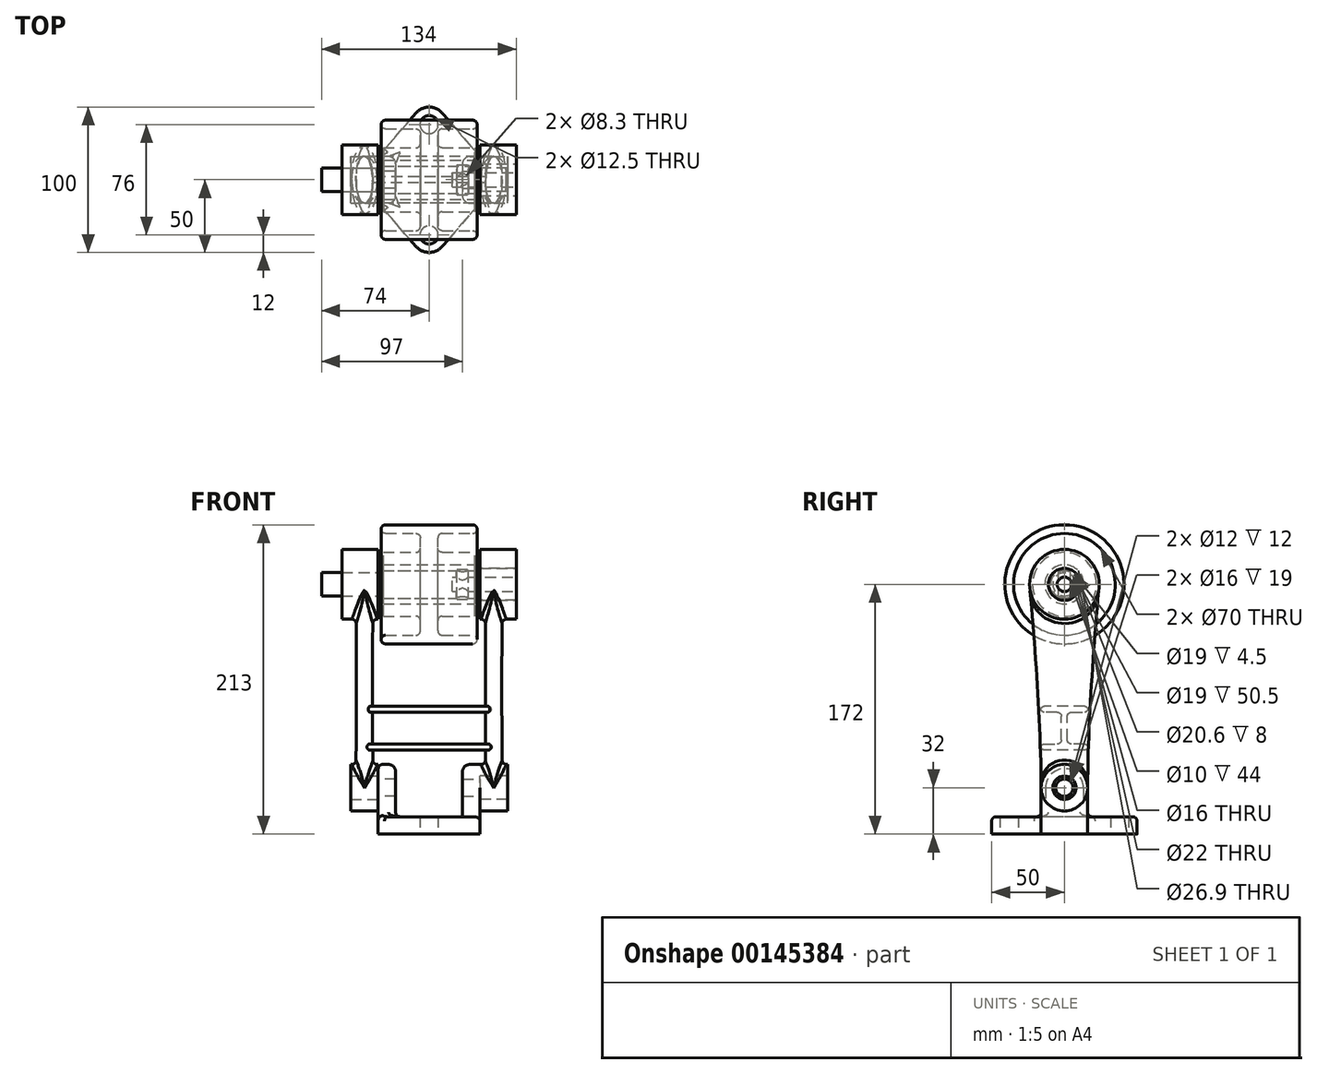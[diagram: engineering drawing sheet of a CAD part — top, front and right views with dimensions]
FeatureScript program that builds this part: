
annotation { "Feature Type Name" : "Feature", "Feature Type Description" : "" }
export const myFeature = defineFeature(function(context is Context, id is Id, definition is map)
    precondition{}
    {
        {
            var Q0;
            Q0=qCreatedBy(makeId("Top.planeOp"),FACE);
            var sketch = newSketch(context, id + "F0", { "sketchPlane" : qUnion([Q0])});
            skLineSegment(sketch, "E0", {"start": v(-9.06, -45.87) * mm, "end": v(-35, -16) * mm});
            skLineSegment(sketch, "E1", {"start": v(-35, 16) * mm, "end": v(-9.06, 45.87) * mm});
            skLineSegment(sketch, "E2", {"start": v(9.06, 45.87) * mm, "end": v(35, 16) * mm});
            skLineSegment(sketch, "E3", {"start": v(35, -16) * mm, "end": v(9.06, -45.87) * mm});
            skLineSegment(sketch, "E4", {"start": v(35, -16) * mm, "end": v(35, 16) * mm});
            skLineSegment(sketch, "E5", {"start": v(-35, -16) * mm, "end": v(-35, 16) * mm});
            skPoint(sketch, "E6.orphan", {"position": v(-48.9, 0) * mm});
            skPoint(sketch, "E7.orphan", {"position": v(48.9, 0) * mm});
            skPoint(sketch, "E8.visualSharp", {"position": v(0, -56.3) * mm});
            skArc(sketch, "E8.filletArc", {"start": v(-9.06, -45.87) * mm, "mid": v(0, -50) * mm, "end": v(9.06, -45.87) * mm});
            skPoint(sketch, "E9.visualSharp", {"position": v(0, 56.3) * mm});
            skArc(sketch, "E9.filletArc", {"start": v(9.06, 45.87) * mm, "mid": v(0, 50) * mm, "end": v(-9.06, 45.87) * mm});
            skCircle(sketch, "E10", {"center": v(0, -38) * mm, "radius": 6.25 * mm});
            skCircle(sketch, "E11", {"center": v(0, 38) * mm, "radius": 6.25 * mm});
            skSolve(sketch);
        }
        {
            var Q0;
            Q0=qSketchRegion(id+"F0",true);
            extrude(context, id + "F1", {"entities" : qUnion([Q0]), "depth" : 12 * mm});
        }
        {
            var Q0;
            Q0=makeQuery(id+"F1.opExtrude","SWEPT_FACE",FACE,{"disambiguationData":[OSD([sQuery(id+"F0.wireOp",EDGE,"E5")])]});
            var sketch = newSketch(context, id + "F2", { "sketchPlane" : qUnion([Q0])});
            skLineSegment(sketch, "E12", {"start": v(-16, 0) * mm, "end": v(-16, 32) * mm});
            skLineSegment(sketch, "E13", {"start": v(16, 0) * mm, "end": v(16, 32) * mm});
            skArc(sketch, "E14", {"start": v(16, 32) * mm, "mid": v(0, 48) * mm, "end": v(-16, 32) * mm});
            skLineSegment(sketch, "E15", {"start": v(-16, 0) * mm, "end": v(16, 0) * mm});
            skCircle(sketch, "E16", {"center": v(0, 32) * mm, "radius": 6 * mm});
            skSolve(sketch);
        }
        {
            var Q0;
            Q0=qSketchRegion(id+"F2",true);
            extrude(context, id + "F3", {"entities" : qUnion([Q0]), "operationType" : NewBodyOperationType.ADD, "oppositeDirection" : true, "depth" : 12 * mm});
        }
        {
            var Q0;
            Q0=makeQuery(id+"F1.opExtrude","SWEPT_BODY",BODY,{"disambiguationData":[OSD([sQuery(id+"F0.wireOp",EDGE,"E0"),sQuery(id+"F0.wireOp",EDGE,"E1"),sQuery(id+"F0.wireOp",EDGE,"E2"),sQuery(id+"F0.wireOp",EDGE,"E3"),sQuery(id+"F0.wireOp",EDGE,"E4"),sQuery(id+"F0.wireOp",EDGE,"E5"),sQuery(id+"F0.wireOp",EDGE,"E8.filletArc"),sQuery(id+"F0.wireOp",EDGE,"E9.filletArc"),sQuery(id+"F0.wireOp",EDGE,"E10"),sQuery(id+"F0.wireOp",EDGE,"E11")])]});
            var Q1;
            Q1=qCreatedBy(makeId("Right.planeOp"),FACE);
            mirror(context, id + "F4", {"operationType" : NewBodyOperationType.ADD, "entities" : qUnion([Q0]), "mirrorPlane" : qUnion([Q1])});
        }
        {
            var Q0;
            Q0=makeQuery(id+"F4.opPattern","COPY",EDGE,{"derivedFrom":makeQuery(id+"F3.boolean.opBoolean","INTERSECT",EDGE,{"derivedFrom":[makeQuery(id+"F1.opExtrude","CAP_FACE",FACE,{"disambiguationData":[OSD([sQuery(id+"F0.wireOp",EDGE,"E0"),sQuery(id+"F0.wireOp",EDGE,"E1"),sQuery(id+"F0.wireOp",EDGE,"E2"),sQuery(id+"F0.wireOp",EDGE,"E3"),sQuery(id+"F0.wireOp",EDGE,"E4"),sQuery(id+"F0.wireOp",EDGE,"E5"),sQuery(id+"F0.wireOp",EDGE,"E8.filletArc"),sQuery(id+"F0.wireOp",EDGE,"E9.filletArc"),sQuery(id+"F0.wireOp",EDGE,"E10"),sQuery(id+"F0.wireOp",EDGE,"E11")])],"isStart":false}),makeQuery(id+"F3.opExtrude","SWEPT_FACE",FACE,{"disambiguationData":[OSD([sQuery(id+"F2.wireOp",EDGE,"E12")])]})]}),"instanceName":"1"});
            var Q1;
            Q1=makeQuery(id+"F4.opPattern","COPY",EDGE,{"derivedFrom":makeQuery(id+"F3.boolean.opBoolean","INTERSECT",EDGE,{"derivedFrom":[makeQuery(id+"F1.opExtrude","CAP_FACE",FACE,{"disambiguationData":[OSD([sQuery(id+"F0.wireOp",EDGE,"E0"),sQuery(id+"F0.wireOp",EDGE,"E1"),sQuery(id+"F0.wireOp",EDGE,"E2"),sQuery(id+"F0.wireOp",EDGE,"E3"),sQuery(id+"F0.wireOp",EDGE,"E4"),sQuery(id+"F0.wireOp",EDGE,"E5"),sQuery(id+"F0.wireOp",EDGE,"E8.filletArc"),sQuery(id+"F0.wireOp",EDGE,"E9.filletArc"),sQuery(id+"F0.wireOp",EDGE,"E10"),sQuery(id+"F0.wireOp",EDGE,"E11")])],"isStart":false}),makeQuery(id+"F3.opExtrude","CAP_FACE",FACE,{"disambiguationData":[OSD([sQuery(id+"F2.wireOp",EDGE,"E12"),sQuery(id+"F2.wireOp",EDGE,"E13"),sQuery(id+"F2.wireOp",EDGE,"E14"),sQuery(id+"F2.wireOp",EDGE,"E15"),sQuery(id+"F2.wireOp",EDGE,"E16")])],"isStart":false})]}),"instanceName":"1"});
            var Q2;
            Q2=makeQuery(id+"F4.opPattern","COPY",EDGE,{"derivedFrom":makeQuery(id+"F3.boolean.opBoolean","INTERSECT",EDGE,{"derivedFrom":[makeQuery(id+"F1.opExtrude","CAP_FACE",FACE,{"disambiguationData":[OSD([sQuery(id+"F0.wireOp",EDGE,"E0"),sQuery(id+"F0.wireOp",EDGE,"E1"),sQuery(id+"F0.wireOp",EDGE,"E2"),sQuery(id+"F0.wireOp",EDGE,"E3"),sQuery(id+"F0.wireOp",EDGE,"E4"),sQuery(id+"F0.wireOp",EDGE,"E5"),sQuery(id+"F0.wireOp",EDGE,"E8.filletArc"),sQuery(id+"F0.wireOp",EDGE,"E9.filletArc"),sQuery(id+"F0.wireOp",EDGE,"E10"),sQuery(id+"F0.wireOp",EDGE,"E11")])],"isStart":false}),makeQuery(id+"F3.opExtrude","SWEPT_FACE",FACE,{"disambiguationData":[OSD([sQuery(id+"F2.wireOp",EDGE,"E13")])]})]}),"instanceName":"1"});
            var Q3;
            Q3=makeQuery(id+"F3.boolean.opBoolean","INTERSECT",EDGE,{"derivedFrom":[makeQuery(id+"F1.opExtrude","CAP_FACE",FACE,{"disambiguationData":[OSD([sQuery(id+"F0.wireOp",EDGE,"E0"),sQuery(id+"F0.wireOp",EDGE,"E1"),sQuery(id+"F0.wireOp",EDGE,"E2"),sQuery(id+"F0.wireOp",EDGE,"E3"),sQuery(id+"F0.wireOp",EDGE,"E4"),sQuery(id+"F0.wireOp",EDGE,"E5"),sQuery(id+"F0.wireOp",EDGE,"E8.filletArc"),sQuery(id+"F0.wireOp",EDGE,"E9.filletArc"),sQuery(id+"F0.wireOp",EDGE,"E10"),sQuery(id+"F0.wireOp",EDGE,"E11")])],"isStart":false}),makeQuery(id+"F3.opExtrude","SWEPT_FACE",FACE,{"disambiguationData":[OSD([sQuery(id+"F2.wireOp",EDGE,"E13")])]})]});
            var Q4;
            Q4=makeQuery(id+"F3.boolean.opBoolean","INTERSECT",EDGE,{"derivedFrom":[makeQuery(id+"F1.opExtrude","CAP_FACE",FACE,{"disambiguationData":[OSD([sQuery(id+"F0.wireOp",EDGE,"E0"),sQuery(id+"F0.wireOp",EDGE,"E1"),sQuery(id+"F0.wireOp",EDGE,"E2"),sQuery(id+"F0.wireOp",EDGE,"E3"),sQuery(id+"F0.wireOp",EDGE,"E4"),sQuery(id+"F0.wireOp",EDGE,"E5"),sQuery(id+"F0.wireOp",EDGE,"E8.filletArc"),sQuery(id+"F0.wireOp",EDGE,"E9.filletArc"),sQuery(id+"F0.wireOp",EDGE,"E10"),sQuery(id+"F0.wireOp",EDGE,"E11")])],"isStart":false}),makeQuery(id+"F3.opExtrude","CAP_FACE",FACE,{"disambiguationData":[OSD([sQuery(id+"F2.wireOp",EDGE,"E12"),sQuery(id+"F2.wireOp",EDGE,"E13"),sQuery(id+"F2.wireOp",EDGE,"E14"),sQuery(id+"F2.wireOp",EDGE,"E15"),sQuery(id+"F2.wireOp",EDGE,"E16")])],"isStart":false})]});
            var Q5;
            Q5=makeQuery(id+"F3.boolean.opBoolean","INTERSECT",EDGE,{"derivedFrom":[makeQuery(id+"F1.opExtrude","CAP_FACE",FACE,{"disambiguationData":[OSD([sQuery(id+"F0.wireOp",EDGE,"E0"),sQuery(id+"F0.wireOp",EDGE,"E1"),sQuery(id+"F0.wireOp",EDGE,"E2"),sQuery(id+"F0.wireOp",EDGE,"E3"),sQuery(id+"F0.wireOp",EDGE,"E4"),sQuery(id+"F0.wireOp",EDGE,"E5"),sQuery(id+"F0.wireOp",EDGE,"E8.filletArc"),sQuery(id+"F0.wireOp",EDGE,"E9.filletArc"),sQuery(id+"F0.wireOp",EDGE,"E10"),sQuery(id+"F0.wireOp",EDGE,"E11")])],"isStart":false}),makeQuery(id+"F3.opExtrude","SWEPT_FACE",FACE,{"disambiguationData":[OSD([sQuery(id+"F2.wireOp",EDGE,"E12")])]})]});
            fillet(context, id + "F5", {"entities" : qUnion([Q0, Q1, Q2, Q3, Q4, Q5]), "radius" : 3 * mm, "tangentPropagation" : true, "allowEdgeOverflow" : false});
        }
        {
            var Q0;
            Q0=makeQuery(id+"F1.opExtrude","CAP_EDGE",EDGE,{"disambiguationData":[OSD([sQuery(id+"F0.wireOp",EDGE,"E1")])],"isStart":false});
            var Q1;
            Q1=makeQuery(id+"F1.opExtrude","CAP_EDGE",EDGE,{"disambiguationData":[OSD([sQuery(id+"F0.wireOp",EDGE,"E0")])],"isStart":false});
            fillet(context, id + "F6", {"entities" : qUnion([Q0, Q1]), "radius" : 3 * mm, "tangentPropagation" : true, "allowEdgeOverflow" : false});
        }
        {
            var Q0;
            Q0=makeQuery(id+"F4.opPattern","COPY",EDGE,{"derivedFrom":makeQuery(id+"F3.opExtrude","CAP_EDGE",EDGE,{"disambiguationData":[OSD([sQuery(id+"F2.wireOp",EDGE,"E14")])],"isStart":false}),"instanceName":"1"});
            var Q1;
            Q1=makeQuery(id+"F3.opExtrude","CAP_EDGE",EDGE,{"disambiguationData":[OSD([sQuery(id+"F2.wireOp",EDGE,"E14")])],"isStart":false});
            fillet(context, id + "F7", {"entities" : qUnion([Q0, Q1]), "radius" : 5 * mm, "tangentPropagation" : true, "allowEdgeOverflow" : false});
        }
        {
            var Q0;
            Q0=makeQuery(id+"F4.boolean.opBoolean","MERGE",FACE,{"derivedFrom":[makeQuery(id+"F1.opExtrude","SWEPT_FACE",FACE,{"disambiguationData":[OSD([sQuery(id+"F0.wireOp",EDGE,"E4")])]}),makeQuery(id+"F4.opPattern","COPY",FACE,{"derivedFrom":makeQuery(id+"F3.boolean.opBoolean","MERGE",FACE,{"derivedFrom":[makeQuery(id+"F1.opExtrude","SWEPT_FACE",FACE,{"disambiguationData":[OSD([sQuery(id+"F0.wireOp",EDGE,"E5")])]}),makeQuery(id+"F3.opExtrude","CAP_FACE",FACE,{"disambiguationData":[OSD([sQuery(id+"F2.wireOp",EDGE,"E12"),sQuery(id+"F2.wireOp",EDGE,"E13"),sQuery(id+"F2.wireOp",EDGE,"E14"),sQuery(id+"F2.wireOp",EDGE,"E15"),sQuery(id+"F2.wireOp",EDGE,"E16")])],"isStart":true})]}),"instanceName":"1"})]});
            var sketch = newSketch(context, id + "F8", { "sketchPlane" : qUnion([Q0])});
            skCircle(sketch, "E17", {"center": v(0, 32) * mm, "radius": 8 * mm});
            skCircle(sketch, "E18", {"center": v(0, 32) * mm, "radius": 16 * mm});
            skSolve(sketch);
        }
        {
            var Q0;
            Q0=qSketchRegion(id+"F8",true);
            extrude(context, id + "F9", {"entities" : qUnion([Q0]), "depth" : 19 * mm});
        }
        {
            var Q0;
            Q0=makeQuery(id+"F4.boolean.opBoolean","MERGE",FACE,{"derivedFrom":[makeQuery(id+"F1.opExtrude","SWEPT_FACE",FACE,{"disambiguationData":[OSD([sQuery(id+"F0.wireOp",EDGE,"E4")])]}),makeQuery(id+"F4.opPattern","COPY",FACE,{"derivedFrom":makeQuery(id+"F3.boolean.opBoolean","MERGE",FACE,{"derivedFrom":[makeQuery(id+"F1.opExtrude","SWEPT_FACE",FACE,{"disambiguationData":[OSD([sQuery(id+"F0.wireOp",EDGE,"E5")])]}),makeQuery(id+"F3.opExtrude","CAP_FACE",FACE,{"disambiguationData":[OSD([sQuery(id+"F2.wireOp",EDGE,"E12"),sQuery(id+"F2.wireOp",EDGE,"E13"),sQuery(id+"F2.wireOp",EDGE,"E14"),sQuery(id+"F2.wireOp",EDGE,"E15"),sQuery(id+"F2.wireOp",EDGE,"E16")])],"isStart":true})]}),"instanceName":"1"})]});
            var sketch = newSketch(context, id + "F10", { "sketchPlane" : qUnion([Q0])});
            skCircle(sketch, "E19", {"center": v(0, 172) * mm, "radius": 8 * mm});
            skCircle(sketch, "E20", {"center": v(0, 172) * mm, "radius": 24 * mm});
            skSolve(sketch);
        }
        {
            var Q0;
            Q0=qSketchRegion(id+"F10",true);
            extrude(context, id + "F11", {"entities" : qUnion([Q0]), "depth" : 25 * mm});
        }
        {
            var Q0;
            Q0=qCreatedBy(makeId("Top.planeOp"),FACE);
            var Q1;
            Q1=sQuery(id+"F2.wireOp",VERTEX,"E14.center");
            cPlane(context, id + "F12", {"entities" : qUnion([Q0, Q1]), "cplaneType" : CPlaneType.PLANE_POINT, "offset" : 25 * mm, "width" : 150 * mm, "height" : 150 * mm});
        }
        {
            var Q0;
            Q0=qCreatedBy(id+"F12.planeOp",FACE);
            var sketch = newSketch(context, id + "F13", { "sketchPlane" : qUnion([Q0])});
            skEllipse(sketch, "E21", {"center": v(44.5, 0) * mm, "majorRadius": 16 * mm, "minorRadius": 6 * mm, "majorAxis": v(0, -1)});
            skSolve(sketch);
        }
        {
            var Q0;
            Q0=makeQuery(id+"F4.boolean.opBoolean","MERGE",FACE,{"derivedFrom":[makeQuery(id+"F1.opExtrude","SWEPT_FACE",FACE,{"disambiguationData":[OSD([sQuery(id+"F0.wireOp",EDGE,"E4")])]}),makeQuery(id+"F4.opPattern","COPY",FACE,{"derivedFrom":makeQuery(id+"F3.boolean.opBoolean","MERGE",FACE,{"derivedFrom":[makeQuery(id+"F1.opExtrude","SWEPT_FACE",FACE,{"disambiguationData":[OSD([sQuery(id+"F0.wireOp",EDGE,"E5")])]}),makeQuery(id+"F3.opExtrude","CAP_FACE",FACE,{"disambiguationData":[OSD([sQuery(id+"F2.wireOp",EDGE,"E12"),sQuery(id+"F2.wireOp",EDGE,"E13"),sQuery(id+"F2.wireOp",EDGE,"E14"),sQuery(id+"F2.wireOp",EDGE,"E15"),sQuery(id+"F2.wireOp",EDGE,"E16")])],"isStart":true})]}),"instanceName":"1"})]});
            var sketch = newSketch(context, id + "F14", { "sketchPlane" : qUnion([Q0])});
            skCircle(sketch, "E22.0", {"center": v(0, 32) * mm, "radius": 8 * mm});
            skSolve(sketch);
        }
        {
            var Q0;
            Q0=makeQuery(id+"F14.imprint","IMPRINT",FACE,{"disambiguationData":[TD([[makeQuery(id+"F14.imprint","IMPRINT",EDGE,{"derivedFrom":sQuery(id+"F14.wireOp",EDGE,"E22.0")}),-1.0]])]});
            var sketch = newSketch(context, id + "F15", { "sketchPlane" : qUnion([Q0])});
            skCircle(sketch, "E23.0", {"center": v(0, 32) * mm, "radius": 8 * mm});
            skSolve(sketch);
        }
        {
            var Q0;
            Q0=qSketchRegion(id+"F15",true);
            extrude(context, id + "F16", {"entities" : qUnion([Q0]), "operationType" : NewBodyOperationType.REMOVE, "depth" : 25 * mm});
        }
        {
            var Q0;
            Q0=qCreatedBy(id+"F12.planeOp",FACE);
            var Q1;
            Q1=sQuery(id+"F10.wireOp",VERTEX,"E19.center");
            cPlane(context, id + "F17", {"entities" : qUnion([Q0, Q1]), "cplaneType" : CPlaneType.PLANE_POINT, "offset" : 25 * mm, "width" : 150 * mm, "height" : 150 * mm});
        }
        {
            var Q0;
            Q0=qCreatedBy(id+"F17.planeOp",FACE);
            var sketch = newSketch(context, id + "F18", { "sketchPlane" : qUnion([Q0])});
            skEllipse(sketch, "E24", {"center": v(44.5, 0) * mm, "majorRadius": 24 * mm, "minorRadius": 6 * mm, "majorAxis": v(0, 1)});
            skSolve(sketch);
        }
        {
            var Q0;
            Q0=qSketchRegion(id+"F13",true);
            var Q1;
            Q1=qSketchRegion(id+"F18",true);
            loft(context, id + "F19", {"operationType" : NewBodyOperationType.ADD, "sheetProfilesArray" : [{ "sheetProfileEntities" : qUnion([Q0]) }, { "sheetProfileEntities" : qUnion([Q1]) }]});
        }
        {
            var Q0;
            Q0=makeQuery(id+"F11.opExtrude","CAP_FACE",FACE,{"disambiguationData":[OSD([sQuery(id+"F10.wireOp",EDGE,"E19"),sQuery(id+"F10.wireOp",EDGE,"E20")])],"isStart":false});
            var sketch = newSketch(context, id + "F20", { "sketchPlane" : qUnion([Q0])});
            skCircle(sketch, "E25.0", {"center": v(0, 172) * mm, "radius": 8 * mm});
            skSolve(sketch);
        }
        {
            var Q0;
            Q0=qSketchRegion(id+"F20",true);
            extrude(context, id + "F21", {"entities" : qUnion([Q0]), "operationType" : NewBodyOperationType.REMOVE, "endBound" : BoundingType.THROUGH_ALL, "oppositeDirection" : true, "depth" : 25 * mm});
        }
        {
            var Q0;
            Q0=makeQuery(id+"F9.opExtrude","CAP_FACE",FACE,{"disambiguationData":[OSD([sQuery(id+"F8.wireOp",EDGE,"E17"),sQuery(id+"F8.wireOp",EDGE,"E18")])],"isStart":true});
            var sketch = newSketch(context, id + "F22", { "sketchPlane" : qUnion([Q0])});
            skCircle(sketch, "E26.0", {"center": v(0, 32) * mm, "radius": 8 * mm});
            skSolve(sketch);
        }
        {
            var Q0;
            Q0=qSketchRegion(id+"F22",true);
            extrude(context, id + "F23", {"entities" : qUnion([Q0]), "operationType" : NewBodyOperationType.REMOVE, "oppositeDirection" : true, "depth" : 25 * mm});
        }
        {
            var Q0;
            Q0=qCreatedBy(makeId("Right.planeOp"),FACE);
            var sketch = newSketch(context, id + "F24", { "sketchPlane" : qUnion([Q0])});
            skLineSegment(sketch, "E27", {"start": v(0, 88) * mm, "end": v(14, 88) * mm});
            skLineSegment(sketch, "E28", {"start": v(14, 84) * mm, "end": v(5, 84) * mm});
            skLineSegment(sketch, "E29", {"start": v(2, 81) * mm, "end": v(2, 65) * mm});
            skLineSegment(sketch, "E30", {"start": v(5, 62) * mm, "end": v(14, 62) * mm});
            skLineSegment(sketch, "E31", {"start": v(14, 58) * mm, "end": v(0, 58) * mm});
            skArc(sketch, "E32", {"start": v(14, 84) * mm, "mid": v(16, 86) * mm, "end": v(14, 88) * mm});
            skArc(sketch, "E33", {"start": v(14, 58) * mm, "mid": v(16, 60) * mm, "end": v(14, 62) * mm});
            skPoint(sketch, "E34.visualSharp", {"position": v(2, 84) * mm});
            skArc(sketch, "E34.filletArc", {"start": v(5, 84) * mm, "mid": v(2.88, 83.12) * mm, "end": v(2, 81) * mm});
            skPoint(sketch, "E35.visualSharp", {"position": v(2, 62) * mm});
            skArc(sketch, "E35.filletArc", {"start": v(2, 65) * mm, "mid": v(2.88, 62.88) * mm, "end": v(5, 62) * mm});
            skPoint(sketch, "E36.visualSharp", {"position": v(-2, 62) * mm});
            skPoint(sketch, "E37.visualSharp", {"position": v(-2, 84) * mm});
            skLineSegment(sketch, "E38", {"start": v(0, 32) * mm, "end": v(0, 94.51) * mm, "construction": true});
            skPoint(sketch, "E39.start.orphan", {"position": v(-16, 88) * mm});
            skPoint(sketch, "E40.end.orphan", {"position": v(-16, 84) * mm});
            skPoint(sketch, "E41.end.orphan", {"position": v(-16, 58) * mm});
            skPoint(sketch, "E41.start.orphan", {"position": v(-16, 62) * mm});
            skArc(sketch, "E42.MirrorCS", {"start": v(-2, 65) * mm, "mid": v(-2.88, 62.88) * mm, "end": v(-5, 62) * mm});
            skArc(sketch, "E43.MirrorCS", {"start": v(-5, 84) * mm, "mid": v(-2.88, 83.12) * mm, "end": v(-2, 81) * mm});
            skPoint(sketch, "E44.MirrorP", {"position": v(16, 84) * mm});
            skArc(sketch, "E45.MirrorCS", {"start": v(-14, 84) * mm, "mid": v(-16, 86) * mm, "end": v(-14, 88) * mm});
            skArc(sketch, "E46.MirrorCS", {"start": v(-14, 58) * mm, "mid": v(-16, 60) * mm, "end": v(-14, 62) * mm});
            skLineSegment(sketch, "E47.MirrorCS", {"start": v(-14, 58) * mm, "end": v(0, 58) * mm});
            skLineSegment(sketch, "E48.MirrorCS", {"start": v(0, 88) * mm, "end": v(-14, 88) * mm});
            skLineSegment(sketch, "E49.MirrorCS", {"start": v(-5, 62) * mm, "end": v(-14, 62) * mm});
            skPoint(sketch, "E50.MirrorP", {"position": v(16, 62) * mm});
            skPoint(sketch, "E51.MirrorP", {"position": v(16, 88) * mm});
            skLineSegment(sketch, "E52.MirrorCS", {"start": v(-2, 81) * mm, "end": v(-2, 65) * mm});
            skLineSegment(sketch, "E53.MirrorCS", {"start": v(-14, 84) * mm, "end": v(-5, 84) * mm});
            skPoint(sketch, "E54.MirrorP", {"position": v(16, 58) * mm});
            skSolve(sketch);
        }
        {
            var Q0;
            Q0=qSketchRegion(id+"F24",true);
            extrude(context, id + "F25", {"entities" : qUnion([Q0]), "operationType" : NewBodyOperationType.ADD, "endBound" : BoundingType.UP_TO_NEXT, "depth" : 25 * mm});
        }
        {
            var Q0;
            Q0=makeQuery(id+"F19.boolean.opBoolean","INTERSECT",EDGE,{"derivedFrom":[makeQuery(id+"F9.opExtrude","SWEPT_FACE",FACE,{"disambiguationData":[OSD([sQuery(id+"F8.wireOp",EDGE,"E18")])]}),makeQuery(id+"F19.opLoft","SWEPT_FACE",FACE,{"disambiguationData":[OSD([sQuery(id+"F13.wireOp",EDGE,"E21"),sQuery(id+"F18.wireOp",EDGE,"E24")])]})]});
            var Q1;
            Q1=makeQuery(id+"F25.opExtrude","TWEAK_EDGE",EDGE,{"derivedFrom":[makeQuery(id+"F19.boolean.opBoolean","SPLIT",FACE,{"disambiguationData":[TD([makeQuery(id+"F9.opExtrude","SWEPT_FACE",FACE,{"disambiguationData":[OSD([sQuery(id+"F8.wireOp",EDGE,"E18")])]}),makeQuery(id+"F11.opExtrude","SWEPT_FACE",FACE,{"disambiguationData":[OSD([sQuery(id+"F10.wireOp",EDGE,"E20")])]})])],"derivedFrom":makeQuery(id+"F19.opLoft","SWEPT_FACE",FACE,{"disambiguationData":[OSD([sQuery(id+"F13.wireOp",EDGE,"E21"),sQuery(id+"F18.wireOp",EDGE,"E24")])]})}),makeQuery(id+"F24.imprint","IMPRINT",EDGE,{"derivedFrom":sQuery(id+"F24.wireOp",EDGE,"E27")}),makeQuery(id+"F24.imprint","IMPRINT",EDGE,{"derivedFrom":sQuery(id+"F24.wireOp",EDGE,"E48.MirrorCS")})]});
            var Q2;
            Q2=makeQuery(id+"F19.boolean.opBoolean","INTERSECT",EDGE,{"derivedFrom":[makeQuery(id+"F11.opExtrude","SWEPT_FACE",FACE,{"disambiguationData":[OSD([sQuery(id+"F10.wireOp",EDGE,"E20")])]}),makeQuery(id+"F19.opLoft","SWEPT_FACE",FACE,{"disambiguationData":[OSD([sQuery(id+"F13.wireOp",EDGE,"E21"),sQuery(id+"F18.wireOp",EDGE,"E24")])]})]});
            fillet(context, id + "F26", {"entities" : qUnion([Q0, Q1, Q2]), "radius" : 3 * mm, "tangentPropagation" : true, "allowEdgeOverflow" : false});
        }
        {
            var Q0;
            Q0=makeQuery(id+"F9.opExtrude","SWEPT_BODY",BODY,{"disambiguationData":[OSD([sQuery(id+"F8.wireOp",EDGE,"E17"),sQuery(id+"F8.wireOp",EDGE,"E18")])]});
            var Q1;
            Q1=qCreatedBy(makeId("Right.planeOp"),FACE);
            mirror(context, id + "F27", {"operationType" : NewBodyOperationType.ADD, "entities" : qUnion([Q0]), "mirrorPlane" : qUnion([Q1])});
        }
        {
            var Q0;
            Q0=makeQuery(id+"F11.opExtrude","CAP_FACE",FACE,{"disambiguationData":[OSD([sQuery(id+"F10.wireOp",EDGE,"E19"),sQuery(id+"F10.wireOp",EDGE,"E20")])],"isStart":true});
            var sketch = newSketch(context, id + "F28", { "sketchPlane" : qUnion([Q0])});
            skCircle(sketch, "E55", {"center": v(0, 172) * mm, "radius": 11 * mm});
            skSolve(sketch);
        }
        {
            var Q0;
            Q0=qSketchRegion(id+"F28",true);
            extrude(context, id + "F29", {"entities" : qUnion([Q0]), "operationType" : NewBodyOperationType.REMOVE, "oppositeDirection" : true, "depth" : 25 * mm});
        }
        {
            var Q0;
            Q0=qCreatedBy(makeId("Front.planeOp"),FACE);
            var sketch = newSketch(context, id + "F30", { "sketchPlane" : qUnion([Q0])});
            skLineSegment(sketch, "E56", {"start": v(-70, 172) * mm, "end": v(107.27, 172) * mm, "construction": true});
            skLineSegment(sketch, "E57", {"start": v(-31.5, 158.55) * mm, "end": v(-31.5, 150) * mm});
            skLineSegment(sketch, "E58", {"start": v(-31.5, 150) * mm, "end": v(-9, 150) * mm});
            skLineSegment(sketch, "E59", {"start": v(-6, 147) * mm, "end": v(-6, 140) * mm});
            skLineSegment(sketch, "E60", {"start": v(-9, 137) * mm, "end": v(-30, 137) * mm});
            skLineSegment(sketch, "E61", {"start": v(-30, 131) * mm, "end": v(0, 131) * mm});
            skArc(sketch, "E62", {"start": v(-30, 137) * mm, "mid": v(-33, 134) * mm, "end": v(-30, 131) * mm});
            skLineSegment(sketch, "E63", {"start": v(0, 122.2) * mm, "end": v(0, 204.02) * mm, "construction": true});
            skLineSegment(sketch, "E64", {"start": v(-31.5, 158.55) * mm, "end": v(0, 158.55) * mm});
            skPoint(sketch, "E65.visualSharp", {"position": v(-6, 150) * mm});
            skArc(sketch, "E65.filletArc", {"start": v(-6, 147) * mm, "mid": v(-6.88, 149.12) * mm, "end": v(-9, 150) * mm});
            skPoint(sketch, "E66.visualSharp", {"position": v(-6, 137) * mm});
            skArc(sketch, "E66.filletArc", {"start": v(-9, 137) * mm, "mid": v(-6.88, 137.88) * mm, "end": v(-6, 140) * mm});
            skArc(sketch, "E67.MirrorCS", {"start": v(9, 137) * mm, "mid": v(6.88, 137.88) * mm, "end": v(6, 140) * mm});
            skArc(sketch, "E68.MirrorCS", {"start": v(6, 147) * mm, "mid": v(6.88, 149.12) * mm, "end": v(9, 150) * mm});
            skLineSegment(sketch, "E69.MirrorCS", {"start": v(6, 147) * mm, "end": v(6, 140) * mm});
            skArc(sketch, "E70.MirrorCS", {"start": v(30, 137) * mm, "mid": v(33, 134) * mm, "end": v(30, 131) * mm});
            skLineSegment(sketch, "E71.MirrorCS", {"start": v(31.5, 158.55) * mm, "end": v(31.5, 150) * mm});
            skPoint(sketch, "E72.MirrorP", {"position": v(6, 137) * mm});
            skPoint(sketch, "E73.MirrorP", {"position": v(6, 150) * mm});
            skLineSegment(sketch, "E74.MirrorCS", {"start": v(30, 131) * mm, "end": v(0, 131) * mm});
            skLineSegment(sketch, "E75.MirrorCS", {"start": v(9, 137) * mm, "end": v(30, 137) * mm});
            skLineSegment(sketch, "E76.MirrorCS", {"start": v(31.5, 158.55) * mm, "end": v(0, 158.55) * mm});
            skLineSegment(sketch, "E77.MirrorCS", {"start": v(31.5, 150) * mm, "end": v(9, 150) * mm});
            skLineSegment(sketch, "E78.MirrorCS", {"start": v(70, 172) * mm, "end": v(-107.27, 172) * mm, "construction": true});
            skSolve(sketch);
        }
        {
            var Q0;
            Q0=qSketchRegion(id+"F30",true);
            var Q1;
            Q1=sQuery(id+"F30.wireOp",EDGE,"E78.MirrorCS");
            revolve(context, id + "F31", {"entities" : qUnion([Q0]), "axis" : qUnion([Q1]), "revolveType" : RevolveType.FULL});
        }
        {
            var Q0;
            Q0=qCreatedBy(makeId("Front.planeOp"),FACE);
            var sketch = newSketch(context, id + "F32", { "sketchPlane" : qUnion([Q0])});
            skLineSegment(sketch, "E79.0", {"start": v(70, 172) * mm, "end": v(-107.27, 172) * mm, "construction": true});
            skLineSegment(sketch, "E80", {"start": v(60, 172) * mm, "end": v(60, 183) * mm});
            skLineSegment(sketch, "E81", {"start": v(60, 183) * mm, "end": v(35, 183) * mm});
            skLineSegment(sketch, "E82", {"start": v(35, 183) * mm, "end": v(35, 181.5) * mm});
            skLineSegment(sketch, "E83", {"start": v(35, 181.5) * mm, "end": v(-35, 181.5) * mm});
            skLineSegment(sketch, "E84", {"start": v(-35, 181.5) * mm, "end": v(-35, 180) * mm});
            skLineSegment(sketch, "E85", {"start": v(-74, 180) * mm, "end": v(-74, 172) * mm});
            skLineSegment(sketch, "E86", {"start": v(-74, 172) * mm, "end": v(60, 172) * mm});
            skLineSegment(sketch, "E87", {"start": v(-74, 180) * mm, "end": v(-35, 180) * mm});
            skSolve(sketch);
        }
        {
            var Q0;
            Q0=qSketchRegion(id+"F32",true);
            var Q1;
            Q1=sQuery(id+"F32.wireOp",EDGE,"E79.0");
            revolve(context, id + "F33", {"entities" : qUnion([Q0]), "axis" : qUnion([Q1]), "revolveType" : RevolveType.FULL});
        }
        {
            var Q0;
            Q0=qCreatedBy(id+"F17.planeOp",FACE);
            var sketch = newSketch(context, id + "F34", { "sketchPlane" : qUnion([Q0])});
            skCircle(sketch, "E88", {"center": v(23, 0) * mm, "radius": 4.15 * mm});
            skSolve(sketch);
        }
        {
            var Q0;
            Q0=qSketchRegion(id+"F34",true);
            var Q1;
            Q1=makeQuery(id+"F33.opRevolve","SWEPT_FACE",FACE,{"disambiguationData":[OSD([sQuery(id+"F32.wireOp",EDGE,"E83")])]});
            var Q2;
            Q2=makeQuery(id+"F33.opRevolve","SWEPT_FACE",FACE,{"disambiguationData":[OSD([sQuery(id+"F32.wireOp",EDGE,"E83")])]});
            extrude(context, id + "F35", {"entities" : qUnion([Q0]), "operationType" : NewBodyOperationType.REMOVE, "endBound" : BoundingType.UP_TO_SURFACE, "oppositeDirection" : true, "endBoundEntityFace" : qUnion([Q1]), "depth" : 25 * mm, "hasSecondDirection" : true, "secondDirectionBound" : SecondDirectionBoundingType.UP_TO_SURFACE, "secondDirectionOppositeDirection" : false, "secondDirectionBoundEntityFace" : qUnion([Q2]), "secondDirectionDepth" : 25 * mm});
        }
        {
            var Q0;
            Q0=makeQuery(id+"F33.opRevolve","SWEPT_FACE",FACE,{"disambiguationData":[OSD([sQuery(id+"F32.wireOp",EDGE,"E80")])]});
            var sketch = newSketch(context, id + "F36", { "sketchPlane" : qUnion([Q0])});
            skCircle(sketch, "E89", {"center": v(0, 172) * mm, "radius": 5 * mm});
            skSolve(sketch);
        }
        {
            var Q0;
            Q0=qSketchRegion(id+"F36",true);
            extrude(context, id + "F37", {"entities" : qUnion([Q0]), "operationType" : NewBodyOperationType.REMOVE, "oppositeDirection" : true, "depth" : 44 * mm});
        }
        {
            var Q0;
            Q0=qCreatedBy(makeId("Front.planeOp"),FACE);
            var sketch = newSketch(context, id + "F38", { "sketchPlane" : qUnion([Q0])});
            skLineSegment(sketch, "E90", {"start": v(72.55, 172) * mm, "end": v(-85.73, 172) * mm, "construction": true});
            skLineSegment(sketch, "E91", {"start": v(-31.5, 185.45) * mm, "end": v(-31.5, 181.5) * mm});
            skLineSegment(sketch, "E92", {"start": v(27, 182.3) * mm, "end": v(27, 181.5) * mm});
            skLineSegment(sketch, "E93", {"start": v(31.5, 181.5) * mm, "end": v(31.5, 185.45) * mm});
            skLineSegment(sketch, "E94", {"start": v(31.5, 185.45) * mm, "end": v(-31.5, 185.45) * mm});
            skLineSegment(sketch, "E95", {"start": v(27, 181.5) * mm, "end": v(31.5, 181.5) * mm});
            skLineSegment(sketch, "E96", {"start": v(27, 182.3) * mm, "end": v(19, 182.3) * mm});
            skLineSegment(sketch, "E97", {"start": v(19, 182.3) * mm, "end": v(19, 181.5) * mm});
            skLineSegment(sketch, "E98", {"start": v(19, 181.5) * mm, "end": v(-31.5, 181.5) * mm});
            skSolve(sketch);
        }
        {
            var Q0;
            Q0=qSketchRegion(id+"F38",true);
            var Q1;
            Q1=sQuery(id+"F38.wireOp",EDGE,"E90");
            revolve(context, id + "F39", {"entities" : qUnion([Q0]), "axis" : qUnion([Q1]), "revolveType" : RevolveType.FULL});
        }
    });
